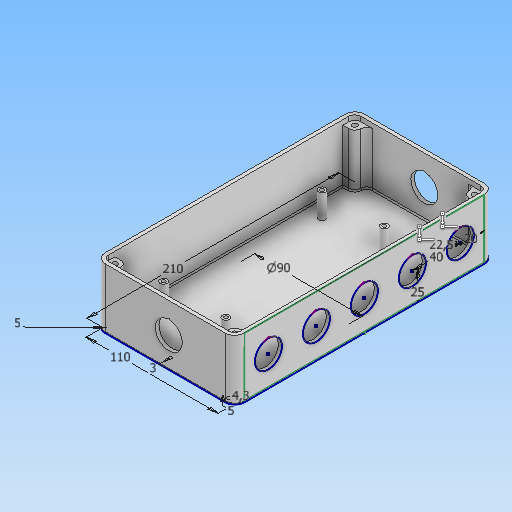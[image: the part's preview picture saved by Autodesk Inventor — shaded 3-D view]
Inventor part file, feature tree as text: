
AUTODESK INVENTOR PART (.ipt)
format: ipt  version: 2025.2 (Build 292293000, 293)  size: 2,344,448 bytes
history: native  units: mm
features: extrude x8, sketch x7, other x4, chamfer x2, mirror x1, projected_geometry x1
ambient origin geometry x8: Origin, YZ Plane, XZ Plane, XY Plane, X Axis, Y Axis, Z Axis, Center Point
bodies: Body1 (feature_tree)
feature tree (23):
  other  "Těleso1"
  other  "PCB"
  sketch  "Náčrt2"
  extrude  "Vysunutí1"  Depth=39.0mm
  extrude  "Vysunutí2"  Depth=40.0mm
  extrude  "Vysunutí4"  Depth=3.5mm
  chamfer  "Zkosení1"  Distance=110.0mm
  chamfer  "Zkosení2"  Distance=45.0mm
  other  "Pracovní rovina1"
  extrude  "Vysunutí8"  Depth=5.0mm
  sketch  "Sketch16"  dims[d4=34.0mm d5=40.0mm]
  sketch  "Sketch17"  dims[d6=45.0mm d7=3.5mm]
  extrude  "Extrusion25"  Depth=20.0mm
  mirror  "Mirror7"
  extrude  "Extrusion26"  Depth=20.0mm
  extrude  "Extrusion27"  Depth=20.0mm
  extrude  "Extrusion28"  Depth=4.0mm
  other  "Obrázek1"
  sketch  "Náčrt6"
  projected_geometry  "Projected Loop8"
  sketch  "Sketch Rectangular Pattern2"  dims[d2=6.0mm d3=39.0mm]
  sketch  "Sketch18"  dims[d8=3.2mm]
  sketch  "Sketch19"  dims[d9=210.0mm d10=110.0mm d11=45.0mm d12=5.0mm d65=80.0mm d66=80.0mm d68=80.0mm d69=4.0mm d70=31.0mm d83=55.5mm d87=144.096001mm d91=66.011253mm d105=30.0mm d106=45.0mm d107=40.0mm d108=30.0mm d110=40.0mm d111=10.0mm d113=10.0mm d116=135.0mm d117=62.0mm d118=10.5mm d120=55.0mm d124=3.0mm d125=2.0mm d126=0.0mm d127=50.0mm d128=0.0mm d136=5.0mm d137=4.3mm d138=46.0mm d139=0.0mm d162=43.0mm d163=53.5mm d164=52.0mm d322=1.0mm d323=2.0mm d324=45.0deg d325=1.0mm d326=2.0mm d327=45.0deg d333=66.0mm d334=0.0mm d509=-10.0mm d525=90.0mm d609=22.5mm d610=25.0mm d611=20.0mm d612=50.0mm d614=40.0mm d615=10.0mm d617=10.0mm d619=22.5mm d621=25.0mm d622=10.0mm d623=0.0mm d624=0.8mm d625=0.0mm d626=0.8mm d627=0.0mm d628=55.0mm d629=12.0mm d631=10.6mm d632=140.0mm d633=60.0mm d637=3.1mm d638=4.0mm d639=4.0mm d640=6.0mm d641=10.0mm d642=3.1mm d643=6.0mm d644=3.1mm d645=6.0mm d646=3.1mm d647=6.0mm d648=4.0mm d649=4.0mm d650=4.0mm d651=4.0mm d652=4.0mm d653=4.0mm d654=20.0mm d655=0.0mm d607=0.0mm d608=0.0mm]
